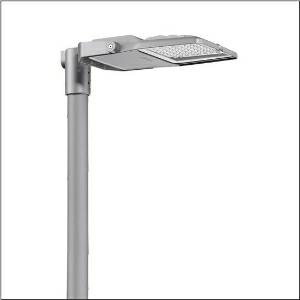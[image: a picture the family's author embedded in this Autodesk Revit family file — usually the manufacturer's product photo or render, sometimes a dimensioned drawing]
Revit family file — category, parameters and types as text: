
# Revit family: floodlight_fl_21_mini___pl43_5xa7775c2a3a_cdc0
name_source: partatom
category: Lighting Fixtures
units: mm (PartAtom-declared; Revit-internal decimal feet)

## family parameters
Cut with Voids When Loaded = No
Host = Face
Light Source = No
Part Type = Normal
Room Calculation Point = No
Round Connector Dimension = Use Diameter
Shared = No

## types (1)
- --- (1 x LED, 12500 lm, 89 W, 3000K)
    Apparent Load = 89 VA
    CIE Flux Codes = 27 78 99 100 100
    Color Rendering = 70
    Color Temperature = 3000K
    Default Elevation = 1800 mm
    Description = Floodlight FL 21 mini, floodlight, primary light control with lens, of PMMA, primary optical cover: protective disc, of toughened safety glass, transparent, light distribution: PL43, light emission: direct distribution, installation type: surface-mounted, LED, High Power LED, rated luminous flux: 12.500lm, luminous efficacy: 140lm/W, light colour: 730, colour temperature: 3000K, control gear: Smart Interface (Zhaga), control: flexible luminous flux parameterisation, time-dependent luminous flux control, constant luminous flux control, overheat protection, pre-setting: logarithmic dimming characteristic, with terminal, 6-pole, mains connection: 220..240V, AC, 50/60Hz, start of lifetime: 89W, end of service life: 94W, reduction: 43W, luminaire housing, of diecast aluminium, powder-coated, Siteco® metallic grey (DB 702S), corrosivity category C5 mid according to DIN EN ISO 12944, suitable for swimming pools, chlorine-resistant, sealing non-destructively replaceable, please order mast flange separately, mast bracket, of steel, galvanised, powder-coated, Siteco® metallic grey (DB 702S), Smart Interface above, protection rating (complete): IP66, insulation class (complete): insulation class II (safety insulation), certification: CE, ENEC, VDE, protection symbol: D, impact resistance: IK08, permissible operating ambient temperature: -40..+40°C, permissible operating ambient temperature for outdoor applications: -40..+50°C, standard: DIN EN 12944, LABS conformity tested according to VDMA 24364:2018-05, packaging unit: 1 piece

Light Distribution: PL43
    Height = 70 mm
    Lamp = 1 x LED
    Lamp Light Flux = 12500 lm
    Lamp Power = 89 W
    Lamp count = 1
    Length = 485 mm
    Luminous efficacy = 140 lm/W
    Manufacturer = Siteco
    ModVariant = No
    Model = 5XA7775C2A3A
    Number of Poles = 1
    OnlyDefault = Yes
    Power Factor = 1
    Product Name = Floodlight FL 21 mini | PL43
    Product group = floodlight | pylon annexe
    ProductGroupID = 6201
    Protection Class = Protection class II
    Protection Degree = IP 66
    RLX_Detail_Level = 1
    RLX_Emergency_Light_Flux = 0 lm
    RLX_Emergency_Type = 0
    RLX_Emergency_Type_DB = No
    RlxData = <blob elided: 100901 chars, md5=20f11ff5>
    Socket = socket
    Standby Power = 0 W
    System Light Flux = 12500 lm
    System Power = 89 W
    Type Comments = factory setting: luminous flux: 100 % | dim-lin: 254 | 456 mA
    Type Image = l_1007125.jpg
    URL = http://relux.com
    VarID = @adj_182571
    Voltage = 0 V
    Weight = 0.00 kg
    Width = 337 mm

## geometry (parser evidence)
native form markers: Blend x4, Sweep x14
no freeform markers — native parametric forms only
